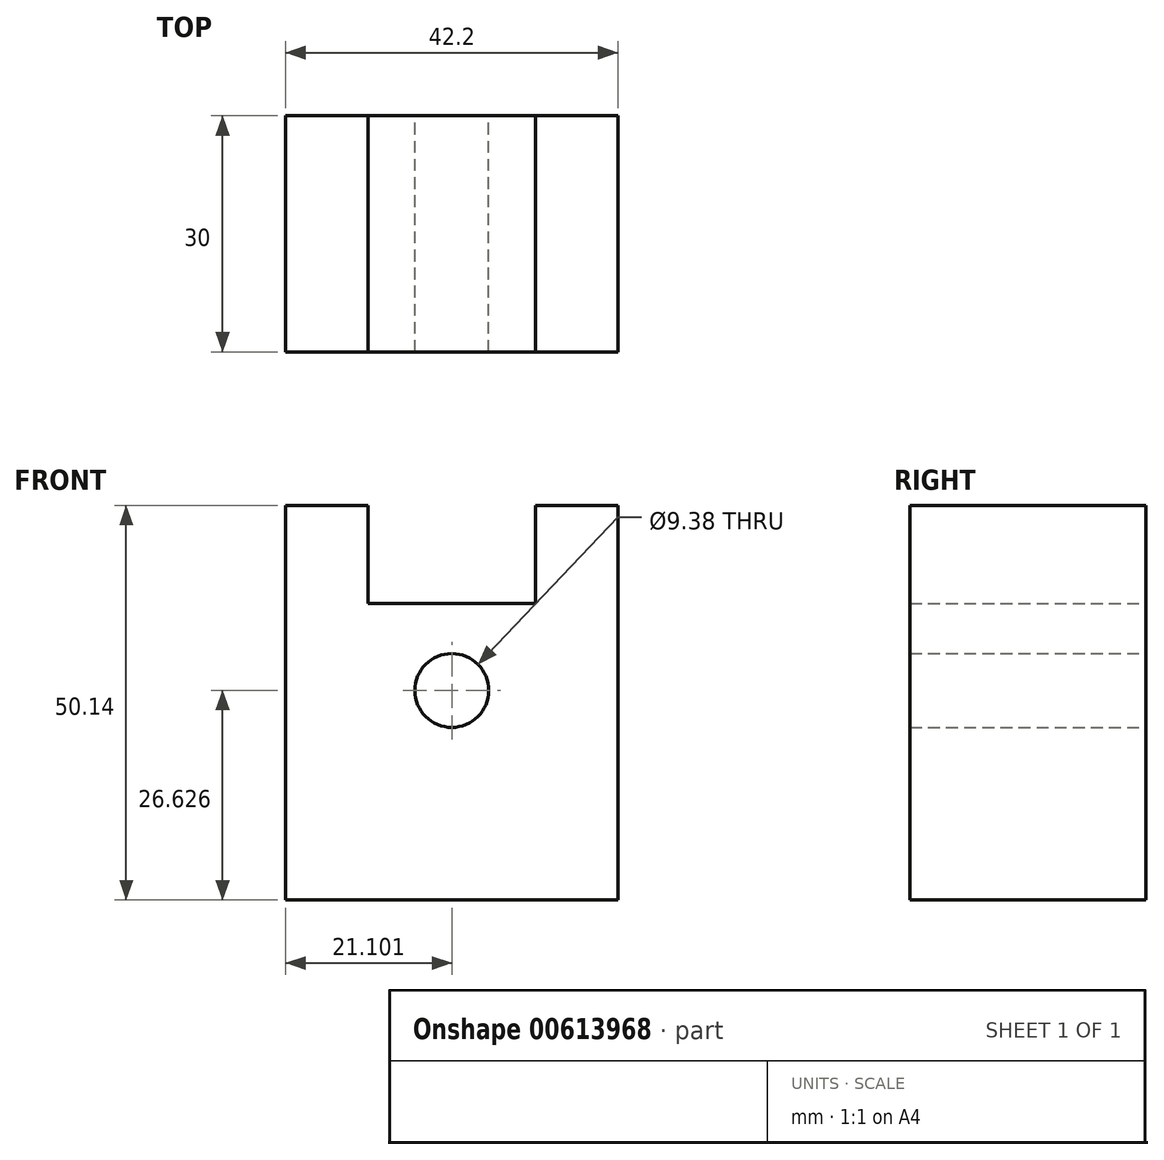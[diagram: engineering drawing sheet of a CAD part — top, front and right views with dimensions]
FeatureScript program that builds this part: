
annotation { "Feature Type Name" : "Feature", "Feature Type Description" : "" }
export const myFeature = defineFeature(function(context is Context, id is Id, definition is map)
    precondition{}
    {
        {
            var Q0;
            Q0=qCreatedBy(makeId("Front.planeOp"),FACE);
            var sketch = newSketch(context, id + "F0", { "sketchPlane" : qUnion([Q0])});
            skLineSegment(sketch, "E0", {"start": v(-14.87, 18.84) * mm, "end": v(-25.35, 18.84) * mm});
            skLineSegment(sketch, "E1", {"start": v(-25.35, 18.84) * mm, "end": v(-25.35, -31.3) * mm});
            skLineSegment(sketch, "E2", {"start": v(-25.35, -31.3) * mm, "end": v(16.85, -31.3) * mm});
            skLineSegment(sketch, "E3", {"start": v(16.85, -31.3) * mm, "end": v(16.85, 18.84) * mm});
            skLineSegment(sketch, "E4", {"start": v(16.85, 18.84) * mm, "end": v(6.37, 18.84) * mm});
            skLineSegment(sketch, "E5", {"start": v(6.37, 18.84) * mm, "end": v(6.37, 6.37) * mm});
            skLineSegment(sketch, "E6", {"start": v(6.37, 6.37) * mm, "end": v(-14.87, 6.37) * mm});
            skLineSegment(sketch, "E7", {"start": v(-14.87, 6.37) * mm, "end": v(-14.87, 18.84) * mm});
            skCircle(sketch, "E8", {"center": v(-4.25, -4.67) * mm, "radius": 4.7 * mm});
            skPoint(sketch, "E8.centerSnap0", {"position": v(-4.25, 6.37) * mm});
            skSolve(sketch);
        }
        {
            var Q0;
            Q0 = qSketchRegion(id + "F0", true);
            extrude(context, id + "F1", {"entities" : qUnion([Q0]), "depth" : 30 * mm, "offsetDistance" : 25 * mm});
        }
    });
